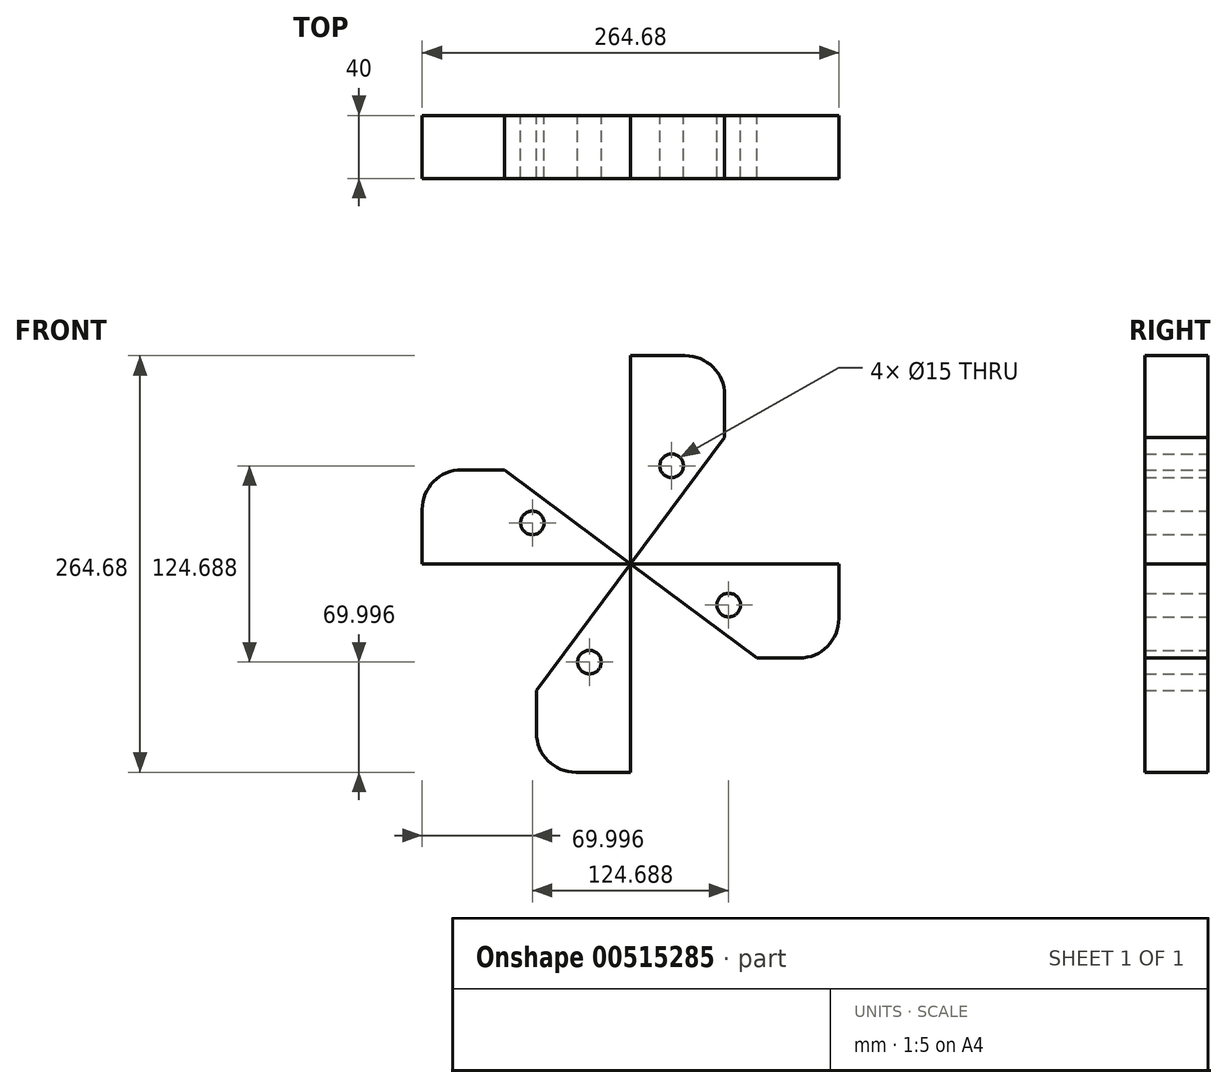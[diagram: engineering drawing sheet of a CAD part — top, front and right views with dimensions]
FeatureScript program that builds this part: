
annotation { "Feature Type Name" : "Feature", "Feature Type Description" : "" }
export const myFeature = defineFeature(function(context is Context, id is Id, definition is map)
    precondition{}
    {
        {
            var Q0;
            Q0=qCreatedBy(makeId("Front.planeOp"),FACE);
            var sketch = newSketch(context, id + "F0", { "sketchPlane" : qUnion([Q0])});
            skLineSegment(sketch, "E0", {"start": v(0, 0) * mm, "end": v(-80.2, 59.73) * mm});
            skLineSegment(sketch, "E1.bottom", {"start": v(-80.2, 59.73) * mm, "end": v(-107.34, 59.73) * mm});
            skLineSegment(sketch, "E1.top", {"start": v(-80.2, 0) * mm, "end": v(-132.34, 0) * mm});
            skLineSegment(sketch, "E1.left", {"start": v(-80.2, 59.73) * mm, "end": v(-80.2, 0) * mm});
            skLineSegment(sketch, "E1.right", {"start": v(-132.34, 34.73) * mm, "end": v(-132.34, 0) * mm});
            skLineSegment(sketch, "E2", {"start": v(-80.2, 0) * mm, "end": v(0, 0) * mm});
            skPoint(sketch, "E3.visualSharp", {"position": v(-132.34, 59.73) * mm});
            skArc(sketch, "E3.filletArc", {"start": v(-107.34, 59.73) * mm, "mid": v(-125.02, 52.41) * mm, "end": v(-132.34, 34.73) * mm});
            skCircle(sketch, "E4", {"center": v(-62.34, 26.1) * mm, "radius": 7.5 * mm});
            skSolve(sketch);
        }
        {
            var Q0;
            Q0 = qSketchRegion(id + "F0", true);
            extrude(context, id + "F1", {"entities" : qUnion([Q0]), "endBound" : BoundingType.SYMMETRIC, "depth" : 40 * mm, "offsetDistance" : 25 * mm});
        }
        {
            var Q0;
            Q0=makeQuery(id+"F1.opExtrude","SWEPT_BODY",BODY,{"disambiguationData":[OSD([sQuery(id+"F0.wireOp",EDGE,"E0"),sQuery(id+"F0.wireOp",EDGE,"E1.bottom"),sQuery(id+"F0.wireOp",EDGE,"E1.top"),sQuery(id+"F0.wireOp",EDGE,"E1.right"),sQuery(id+"F0.wireOp",EDGE,"E2"),sQuery(id+"F0.wireOp",EDGE,"E3.filletArc"),sQuery(id+"F0.wireOp",EDGE,"E4")])]});
            var Q1;
            Q1=makeQuery(id+"F1.opExtrude","SWEPT_EDGE",EDGE,{"disambiguationData":[OSD([sQuery(id+"F0.wireOp",EDGE,"E0"),sQuery(id+"F0.wireOp",EDGE,"E2")])]});
            circularPattern(context, id + "F2", {"entities" : qUnion([Q0]), "axis" : qUnion([Q1]), "angle" : 360 * degree, "instanceCount" : 4, "equalSpace" : true});
        }
    });
